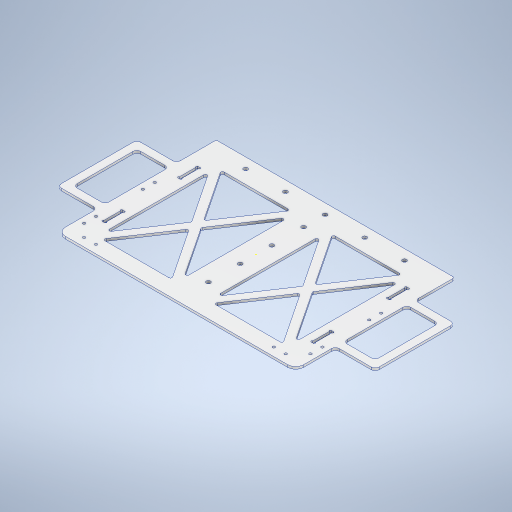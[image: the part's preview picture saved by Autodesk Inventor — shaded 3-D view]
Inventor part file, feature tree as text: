
AUTODESK INVENTOR PART (.ipt)
format: ipt  version: 2024.3 (Build 283343000, 343)  size: 781,824 bytes
history: native  units: mm
features: sketch x9, extrude x6, fillet x4, projected_geometry x3, hole x2, other x1
ambient origin geometry x8: Origin, YZ Plane, XZ Plane, XY Plane, X Axis, Y Axis, Z Axis, Center Point
bodies: Body1 (feature_tree)
feature tree (25):
  other  "ソリッド1"
  extrude  "押し出し1"  Depth=190.0mm
  extrude  "押し出し4"  Depth=300.0mm
  sketch  "スケッチ4"
  extrude  "押し出し13"  Depth=3.0mm TaperAngle=0.0deg
  fillet  "フィレット3"  Radius=142.5mm
  extrude  "押し出し18"  Depth=285.0mm
  extrude  "押し出し19"  Depth=3.2mm
  fillet  "フィレット11"  Radius=3.2mm
  fillet  "フィレット12"  Radius=21.0mm
  fillet  "フィレット13"  Radius=21.0mm
  hole  "穴1"  [1 undecoded]
  hole  "穴2"  [1 undecoded]
  extrude  "押し出し22"  Depth=3.2mm
  sketch  "スケッチ1"
  sketch  "スケッチ2"
  sketch  "スケッチ14"
  projected_geometry  "投影ループ5"
  sketch  "スケッチ19"
  sketch  "スケッチ20"
  projected_geometry  "投影ループ6"
  sketch  "スケッチ21"
  sketch  "スケッチ26"
  sketch  "スケッチ27"
  projected_geometry  "投影ループ9"
note: 2 required parameter values undecoded (feature->parameter linkage not recoverable at this tier; creation-order binding heuristic only, values carry confidence <= 0.55)
